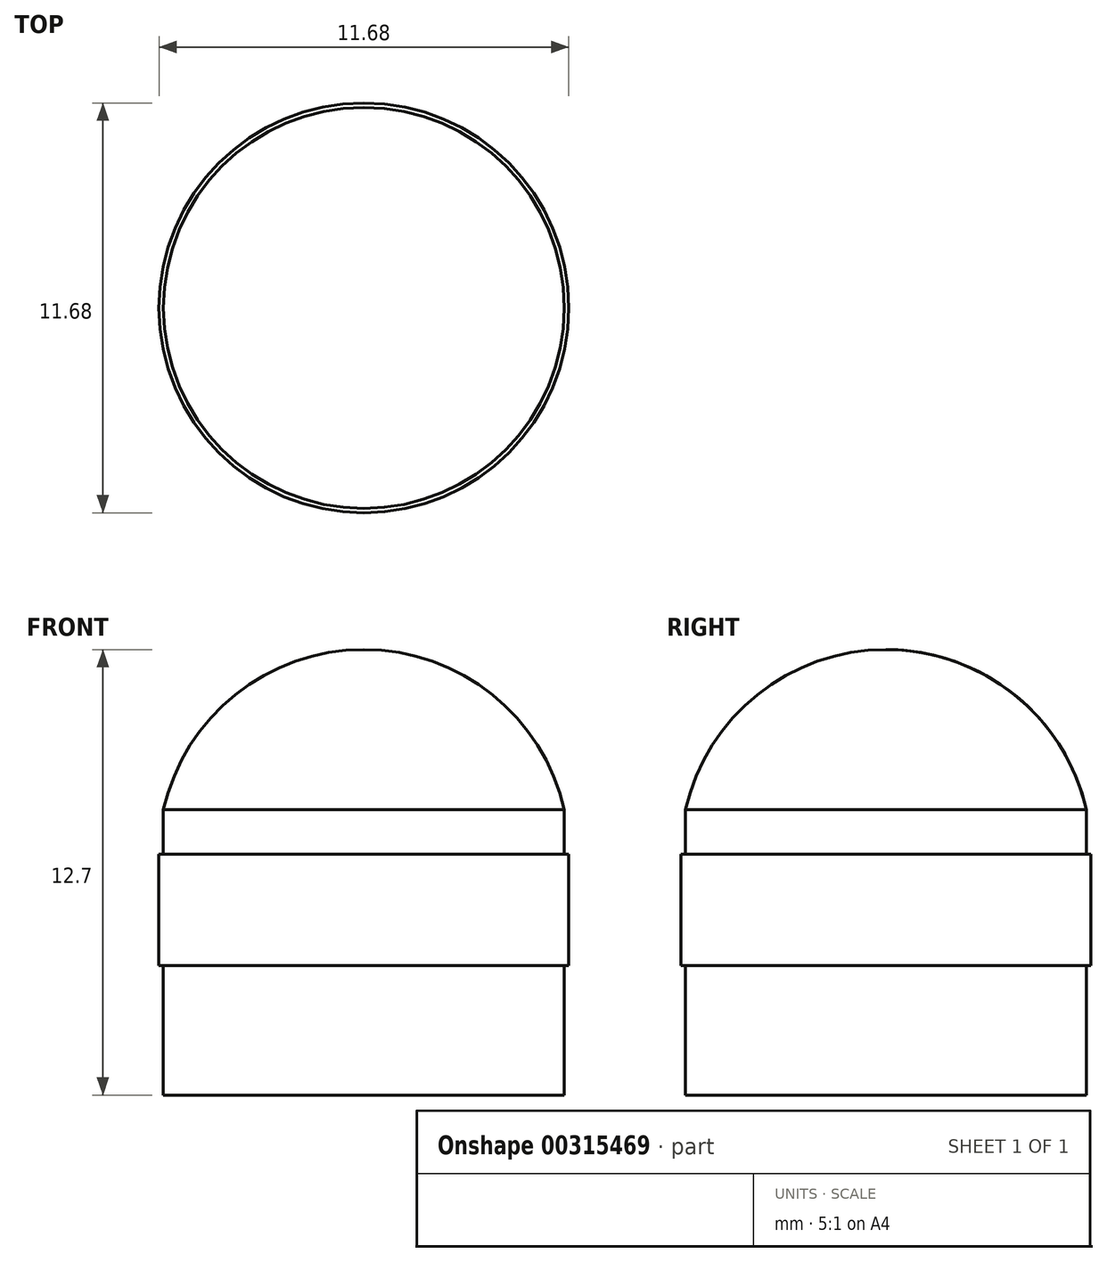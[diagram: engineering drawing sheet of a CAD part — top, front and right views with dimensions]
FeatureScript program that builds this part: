
annotation { "Feature Type Name" : "Feature", "Feature Type Description" : "" }
export const myFeature = defineFeature(function(context is Context, id is Id, definition is map)
    precondition{}
    {
        {
            var Q0;
            Q0=qCreatedBy(makeId("Right.planeOp"),FACE);
            var sketch = newSketch(context, id + "F0", { "sketchPlane" : qUnion([Q0])});
            skLineSegment(sketch, "E0", {"start": v(0, 0) * mm, "end": v(0, 16.26) * mm, "construction": true});
            skLineSegment(sketch, "E1", {"start": v(0, 0) * mm, "end": v(0, -16.85) * mm, "construction": true});
            skLineSegment(sketch, "E2", {"start": v(0, 0) * mm, "end": v(5.72, 0) * mm});
            skLineSegment(sketch, "E3", {"start": v(5.72, 0) * mm, "end": v(5.72, 3.7) * mm});
            skLineSegment(sketch, "E4", {"start": v(5.72, 3.7) * mm, "end": v(5.84, 3.7) * mm});
            skLineSegment(sketch, "E5", {"start": v(5.84, 3.7) * mm, "end": v(5.84, 6.87) * mm});
            skLineSegment(sketch, "E6", {"start": v(5.84, 6.87) * mm, "end": v(5.72, 6.87) * mm});
            skLineSegment(sketch, "E7", {"start": v(0, 12.7) * mm, "end": v(0, 0) * mm});
            skArc(sketch, "E8", {"start": v(5.72, 8.13) * mm, "mid": v(3.66, 11.42) * mm, "end": v(0, 12.7) * mm});
            skPoint(sketch, "E9.start.orphan", {"position": v(0, 8.13) * mm});
            skLineSegment(sketch, "E10", {"start": v(5.71, 6.87) * mm, "end": v(5.71, 8.13) * mm});
            skLineSegment(sketch, "E11", {"start": v(5.71, 8.13) * mm, "end": v(-4.37, 8.13) * mm, "construction": true});
            skSolve(sketch);
        }
        {
            var Q0;
            Q0=makeQuery(id+"F0.imprint","IMPRINT",FACE,{"disambiguationData":[TD([[makeQuery(id+"F0.imprint","IMPRINT",EDGE,{"derivedFrom":sQuery(id+"F0.wireOp",EDGE,"E2")}),1.0]])]});
            var Q1;
            Q1=sQuery(id+"F0.wireOp",EDGE,"E7");
            revolve(context, id + "F1", {"entities" : qUnion([Q0]), "axis" : qUnion([Q1]), "revolveType" : RevolveType.FULL});
        }
    });
